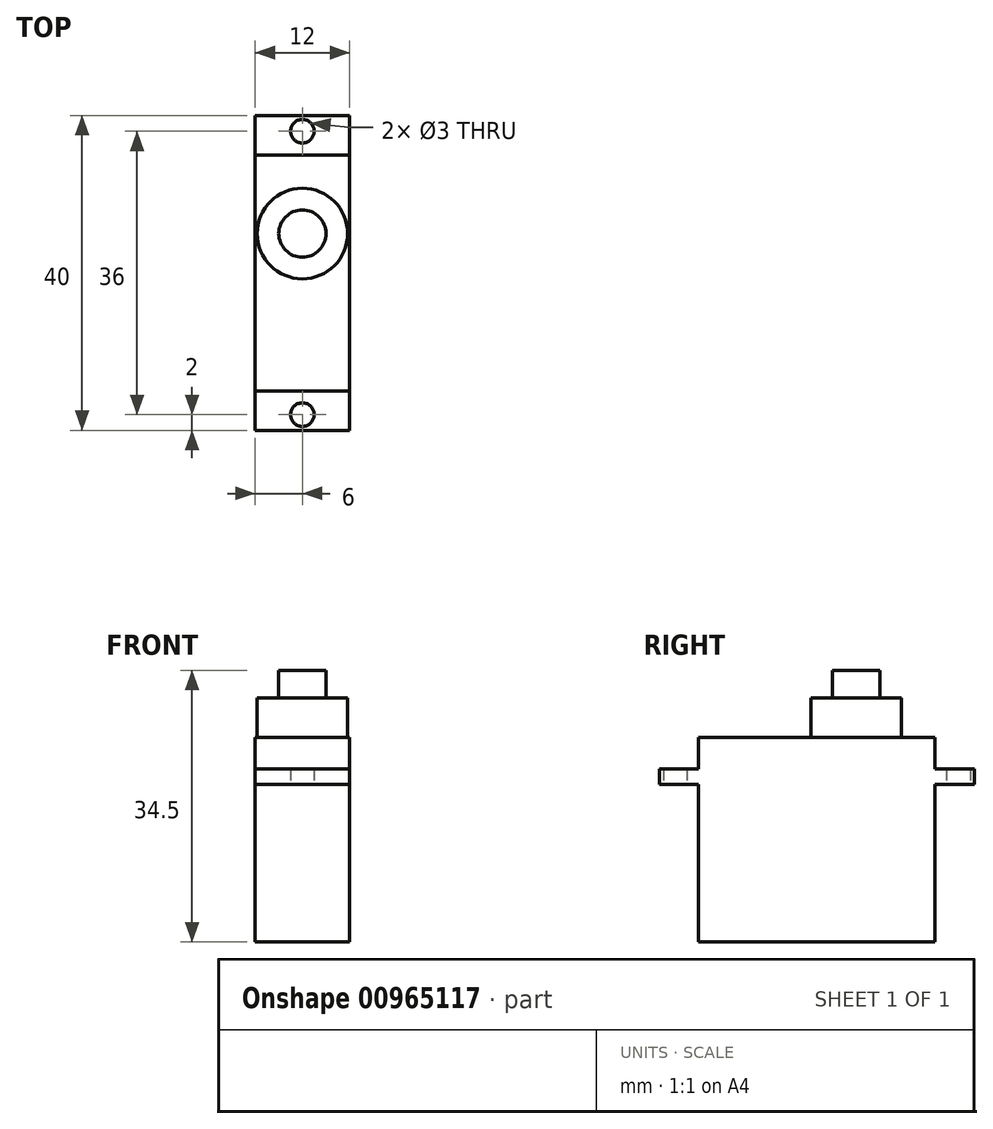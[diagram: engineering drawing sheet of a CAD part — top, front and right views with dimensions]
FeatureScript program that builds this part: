
annotation { "Feature Type Name" : "Feature", "Feature Type Description" : "" }
export const myFeature = defineFeature(function(context is Context, id is Id, definition is map)
    precondition{}
    {
        {
            var Q0;
            Q0=qCreatedBy(makeId("Top.planeOp"),FACE);
            var sketch = newSketch(context, id + "F0", { "sketchPlane" : qUnion([Q0])});
            skLineSegment(sketch, "E0.bottom", {"start": v(0, 0) * mm, "end": v(12, 0) * mm});
            skLineSegment(sketch, "E0.top", {"start": v(0, 40) * mm, "end": v(12, 40) * mm});
            skLineSegment(sketch, "E0.left", {"start": v(0, 0) * mm, "end": v(0, 40) * mm});
            skLineSegment(sketch, "E0.right", {"start": v(12, 0) * mm, "end": v(12, 40) * mm});
            skLineSegment(sketch, "E1", {"start": v(0, 35) * mm, "end": v(12, 35) * mm});
            skLineSegment(sketch, "E2", {"start": v(0, 5) * mm, "end": v(12, 5) * mm});
            skCircle(sketch, "E3", {"center": v(6, 38) * mm, "radius": 1.5 * mm});
            skCircle(sketch, "E4", {"center": v(6, 2) * mm, "radius": 1.5 * mm});
            skSolve(sketch);
        }
        {
            var Q0;
            {var subQ0=sQuery(id+"F0.wireOp",EDGE,"E0.top");Q0=makeQuery(id+"F0.imprint","IMPRINT",FACE,{"disambiguationData":[TD([[makeQuery(id+"F0.imprint","IMPRINT",EDGE,{"derivedFrom":subQ0}),-1.0]])]});}
            var Q1;
            {var subQ0=sQuery(id+"F0.wireOp",EDGE,"E1");Q1=makeQuery(id+"F0.imprint","IMPRINT",FACE,{"disambiguationData":[TD([[makeQuery(id+"F0.imprint","IMPRINT",EDGE,{"derivedFrom":subQ0}),-1.0]])]});}
            var Q2;
            {var subQ0=sQuery(id+"F0.wireOp",EDGE,"E0.bottom");Q2=makeQuery(id+"F0.imprint","IMPRINT",FACE,{"disambiguationData":[TD([[makeQuery(id+"F0.imprint","IMPRINT",EDGE,{"derivedFrom":subQ0}),1.0]])]});}
            extrude(context, id + "F1", {"entities" : qUnion([Q0, Q1, Q2]), "depth" : 2 * mm, "offsetDistance" : 25 * mm});
        }
        {
            var Q0;
            {var subQ0=sQuery(id+"F0.wireOp",EDGE,"E1");Q0=makeQuery(id+"F0.imprint","IMPRINT",FACE,{"disambiguationData":[TD([[makeQuery(id+"F0.imprint","IMPRINT",EDGE,{"derivedFrom":subQ0}),-1.0]])]});}
            extrude(context, id + "F2", {"entities" : qUnion([Q0]), "operationType" : NewBodyOperationType.ADD, "depth" : 6 * mm, "offsetDistance" : 25 * mm});
        }
        {
            var Q0;
            {var subQ0=sQuery(id+"F0.wireOp",EDGE,"E1");Q0=makeQuery(id+"F0.imprint","IMPRINT",FACE,{"disambiguationData":[TD([[makeQuery(id+"F0.imprint","IMPRINT",EDGE,{"derivedFrom":subQ0}),-1.0]])]});}
            extrude(context, id + "F3", {"entities" : qUnion([Q0]), "operationType" : NewBodyOperationType.ADD, "oppositeDirection" : true, "depth" : 20 * mm, "offsetDistance" : 25 * mm});
        }
        {
            var Q0;
            Q0=makeQuery(id+"F2.opExtrude","CAP_FACE",FACE,{"disambiguationData":[OSD([sQuery(id+"F0.wireOp",EDGE,"E0.left"),sQuery(id+"F0.wireOp",EDGE,"E0.right"),sQuery(id+"F0.wireOp",EDGE,"E1"),sQuery(id+"F0.wireOp",EDGE,"E2")])],"isStart":false});
            var sketch = newSketch(context, id + "F4", { "sketchPlane" : qUnion([Q0])});
            skCircle(sketch, "E5", {"center": v(6, 25) * mm, "radius": 3 * mm});
            skCircle(sketch, "E6", {"center": v(6, 25) * mm, "radius": 5.75 * mm});
            skSolve(sketch);
        }
        {
            var Q0;
            Q0=makeQuery(id+"F4.imprint","IMPRINT",FACE,{"disambiguationData":[TD([[makeQuery(id+"F4.imprint","IMPRINT",EDGE,{"derivedFrom":sQuery(id+"F4.wireOp",EDGE,"E5")}),1.0]])]});
            extrude(context, id + "F5", {"entities" : qUnion([Q0]), "operationType" : NewBodyOperationType.ADD, "depth" : 8.5 * mm, "offsetDistance" : 25 * mm});
        }
        {
            var Q0;
            Q0=makeQuery(id+"F4.imprint","IMPRINT",FACE,{"disambiguationData":[TD([[makeQuery(id+"F4.imprint","IMPRINT",EDGE,{"derivedFrom":sQuery(id+"F4.wireOp",EDGE,"E5")}),-1.0]])]});
            extrude(context, id + "F6", {"entities" : qUnion([Q0]), "operationType" : NewBodyOperationType.ADD, "depth" : 5 * mm, "offsetDistance" : 25 * mm});
        }
    });
